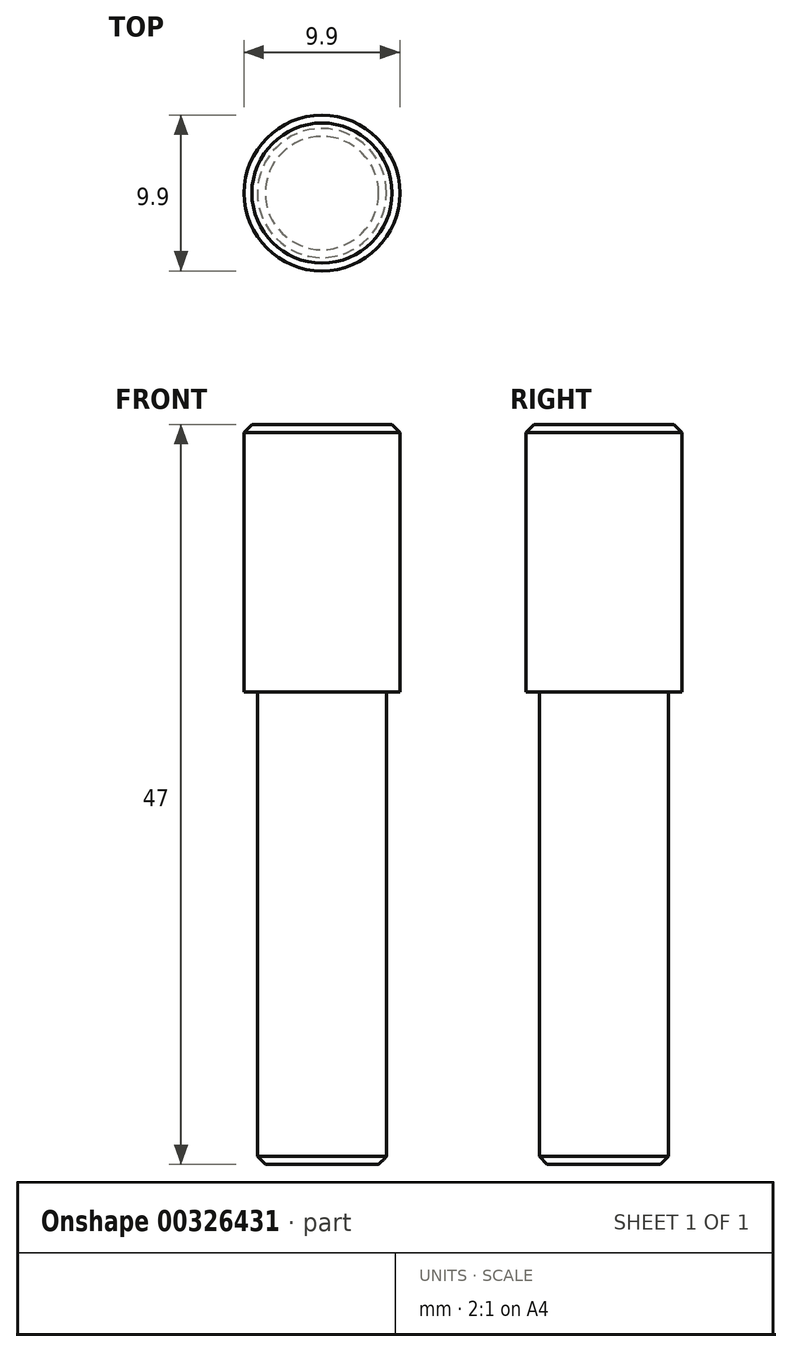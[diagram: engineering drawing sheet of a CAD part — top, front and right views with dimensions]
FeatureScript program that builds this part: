
annotation { "Feature Type Name" : "Feature", "Feature Type Description" : "" }
export const myFeature = defineFeature(function(context is Context, id is Id, definition is map)
    precondition{}
    {
        {
            var Q0;
            Q0=qCreatedBy(makeId("Top.planeOp"),FACE);
            var sketch = newSketch(context, id + "F0", { "sketchPlane" : qUnion([Q0])});
            skCircle(sketch, "E0", {"center": v(0, 0) * mm, "radius": 4.95 * mm});
            skCircle(sketch, "E1.0", {"center": v(0, 0) * mm, "radius": 4.1 * mm});
            skSolve(sketch);
        }
        {
            var Q0;
            Q0 = qSketchRegion(id + "F0", true);
            var Q1;
            Q1=makeQuery(id+"F0.imprint","IMPRINT",FACE,{"disambiguationData":[TD([[makeQuery(id+"F0.imprint","IMPRINT",EDGE,{"derivedFrom":sQuery(id+"F0.wireOp",EDGE,"E1.0")}),1.0]])]});
            extrude(context, id + "F1", {"entities" : qUnion([Q0, Q1]), "depth" : 17 * mm});
        }
        {
            var Q0;
            Q0=makeQuery(id+"F0.imprint","IMPRINT",FACE,{"disambiguationData":[TD([[makeQuery(id+"F0.imprint","IMPRINT",EDGE,{"derivedFrom":sQuery(id+"F0.wireOp",EDGE,"E1.0")}),1.0]])]});
            extrude(context, id + "F2", {"entities" : qUnion([Q0]), "operationType" : NewBodyOperationType.ADD, "oppositeDirection" : true, "depth" : 30 * mm});
        }
        {
            var Q0;
            Q0=makeQuery(id+"F1.opExtrude","CAP_EDGE",EDGE,{"disambiguationData":[OSD([sQuery(id+"F0.wireOp",EDGE,"E0")])],"isStart":false});
            var Q1;
            Q1=makeQuery(id+"F2.opExtrude","CAP_EDGE",EDGE,{"disambiguationData":[OSD([sQuery(id+"F0.wireOp",EDGE,"E1.0")])],"isStart":false});
            chamfer(context, id + "F3", {"entities" : qUnion([Q0, Q1]), "width" : 0.5 * mm, "tangentPropagation" : true});
        }
    });
